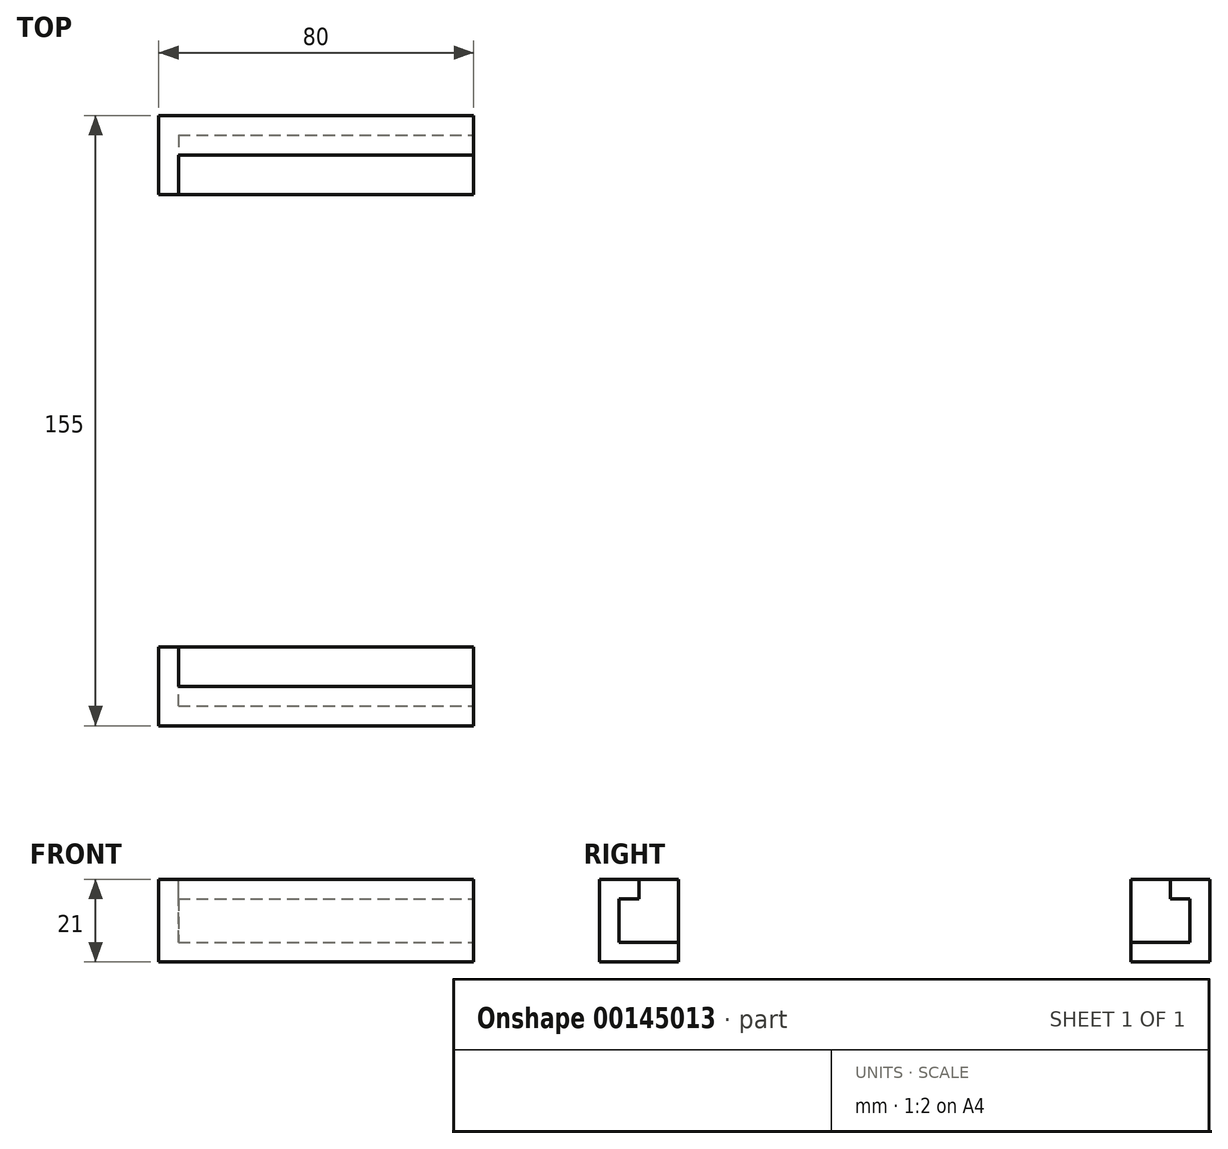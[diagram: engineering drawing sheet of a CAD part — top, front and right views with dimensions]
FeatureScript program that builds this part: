
annotation { "Feature Type Name" : "Feature", "Feature Type Description" : "" }
export const myFeature = defineFeature(function(context is Context, id is Id, definition is map)
    precondition{}
    {
        {
            var Q0;
            Q0=qCreatedBy(makeId("Top.planeOp"),FACE);
            var sketch = newSketch(context, id + "F0", { "sketchPlane" : qUnion([Q0])});
            skLineSegment(sketch, "E0.bottom", {"start": v(37.5, 77.5) * mm, "end": v(-37.5, 77.5) * mm});
            skLineSegment(sketch, "E0.top", {"start": v(37.5, -77.5) * mm, "end": v(-37.5, -77.5) * mm});
            skLineSegment(sketch, "E0.left", {"start": v(37.5, 77.5) * mm, "end": v(37.5, -77.5) * mm});
            skLineSegment(sketch, "E0.right", {"start": v(-37.5, 77.5) * mm, "end": v(-37.5, -77.5) * mm});
            skPoint(sketch, "E0.middle", {"position": v(0, 0) * mm});
            skSolve(sketch);
        }
        {
            var Q0;
            Q0 = qSketchRegion(id + "F0", true);
            extrude(context, id + "F1", {"entities" : qUnion([Q0]), "depth" : 5 * mm});
        }
        {
            var Q0;
            Q0=makeQuery(id+"F1.opExtrude","CAP_FACE",FACE,{"disambiguationData":[OSD([sQuery(id+"F0.wireOp",EDGE,"E0.bottom"),sQuery(id+"F0.wireOp",EDGE,"E0.top"),sQuery(id+"F0.wireOp",EDGE,"E0.left"),sQuery(id+"F0.wireOp",EDGE,"E0.right")])],"isStart":false});
            var sketch = newSketch(context, id + "F2", { "sketchPlane" : qUnion([Q0])});
            skLineSegment(sketch, "E1.bottom", {"start": v(-37.5, -77.5) * mm, "end": v(37.5, -77.5) * mm});
            skLineSegment(sketch, "E1.top", {"start": v(-37.5, -72.5) * mm, "end": v(37.5, -72.5) * mm});
            skLineSegment(sketch, "E1.left", {"start": v(-37.5, -77.5) * mm, "end": v(-37.5, -72.5) * mm});
            skLineSegment(sketch, "E1.right", {"start": v(37.5, -77.5) * mm, "end": v(37.5, -72.5) * mm});
            skSolve(sketch);
        }
        {
            var Q0;
            Q0 = qSketchRegion(id + "F2", true);
            extrude(context, id + "F3", {"entities" : qUnion([Q0]), "operationType" : NewBodyOperationType.ADD, "depth" : 11 * mm});
        }
        {
            var Q0;
            Q0=makeQuery(id+"F3.opExtrude","SWEPT_FACE",FACE,{"disambiguationData":[OSD([sQuery(id+"F2.wireOp",EDGE,"E1.top")])]});
            var sketch = newSketch(context, id + "F4", { "sketchPlane" : qUnion([Q0])});
            skLineSegment(sketch, "E2.bottom", {"start": v(-37.5, 16) * mm, "end": v(37.5, 16) * mm});
            skLineSegment(sketch, "E2.top", {"start": v(-37.5, 21) * mm, "end": v(37.5, 21) * mm});
            skLineSegment(sketch, "E2.left", {"start": v(-37.5, 16) * mm, "end": v(-37.5, 21) * mm});
            skLineSegment(sketch, "E2.right", {"start": v(37.5, 16) * mm, "end": v(37.5, 21) * mm});
            skSolve(sketch);
        }
        {
            var Q0;
            Q0 = qSketchRegion(id + "F4", true);
            extrude(context, id + "F5", {"entities" : qUnion([Q0]), "depth" : 5 * mm});
        }
        {
            var Q0;
            Q0=makeQuery(id+"F5.opExtrude","CAP_FACE",FACE,{"disambiguationData":[OSD([sQuery(id+"F4.wireOp",EDGE,"E2.bottom"),sQuery(id+"F4.wireOp",EDGE,"E2.top"),sQuery(id+"F4.wireOp",EDGE,"E2.left"),sQuery(id+"F4.wireOp",EDGE,"E2.right")])],"isStart":true});
            extrude(context, id + "F6", {"entities" : qUnion([Q0]), "depth" : 5 * mm});
        }
        {
            var Q0;
            Q0=makeQuery(id+"F6.opExtrude","SWEPT_BODY",BODY,{"disambiguationData":[OSD([sQuery(id+"F4.wireOp",EDGE,"E2.bottom"),sQuery(id+"F4.wireOp",EDGE,"E2.top"),sQuery(id+"F4.wireOp",EDGE,"E2.left"),sQuery(id+"F4.wireOp",EDGE,"E2.right")])]});
            var Q1;
            Q1=makeQuery(id+"F5.opExtrude","SWEPT_BODY",BODY,{"disambiguationData":[OSD([sQuery(id+"F4.wireOp",EDGE,"E2.bottom"),sQuery(id+"F4.wireOp",EDGE,"E2.top"),sQuery(id+"F4.wireOp",EDGE,"E2.left"),sQuery(id+"F4.wireOp",EDGE,"E2.right")])]});
            var Q2;
            Q2=makeQuery(id+"F1.opExtrude","SWEPT_BODY",BODY,{"disambiguationData":[OSD([sQuery(id+"F0.wireOp",EDGE,"E0.bottom"),sQuery(id+"F0.wireOp",EDGE,"E0.top"),sQuery(id+"F0.wireOp",EDGE,"E0.left"),sQuery(id+"F0.wireOp",EDGE,"E0.right")])]});
            booleanBodies(context, id + "F7", {"operationType" : BooleanOperationType.UNION, "tools" : qUnion([Q0, Q1, Q2])});
        }
        {
            var Q0;
            Q0=makeQuery(id+"F1.opExtrude","CAP_FACE",FACE,{"disambiguationData":[OSD([sQuery(id+"F0.wireOp",EDGE,"E0.bottom"),sQuery(id+"F0.wireOp",EDGE,"E0.top"),sQuery(id+"F0.wireOp",EDGE,"E0.left"),sQuery(id+"F0.wireOp",EDGE,"E0.right")])],"isStart":false});
            var sketch = newSketch(context, id + "F8", { "sketchPlane" : qUnion([Q0])});
            skLineSegment(sketch, "E3.bottom", {"start": v(-37.5, 77.5) * mm, "end": v(37.5, 77.5) * mm});
            skLineSegment(sketch, "E3.top", {"start": v(-37.5, 72.5) * mm, "end": v(37.5, 72.5) * mm});
            skLineSegment(sketch, "E3.left", {"start": v(-37.5, 77.5) * mm, "end": v(-37.5, 72.5) * mm});
            skLineSegment(sketch, "E3.right", {"start": v(37.5, 77.5) * mm, "end": v(37.5, 72.5) * mm});
            skSolve(sketch);
        }
        {
            var Q0;
            Q0 = qSketchRegion(id + "F8", true);
            extrude(context, id + "F9", {"entities" : qUnion([Q0]), "operationType" : NewBodyOperationType.ADD, "depth" : 11 * mm});
        }
        {
            var Q0;
            Q0=makeQuery(id+"F9.boolean.opBoolean","MERGE",FACE,{"derivedFrom":[makeQuery(id+"F1.opExtrude","SWEPT_FACE",FACE,{"disambiguationData":[OSD([sQuery(id+"F0.wireOp",EDGE,"E0.bottom")])]}),makeQuery(id+"F9.opExtrude","SWEPT_FACE",FACE,{"disambiguationData":[OSD([sQuery(id+"F8.wireOp",EDGE,"E3.bottom")])]})]});
            var sketch = newSketch(context, id + "F10", { "sketchPlane" : qUnion([Q0])});
            skLineSegment(sketch, "E4.bottom", {"start": v(-37.5, 16) * mm, "end": v(37.5, 16) * mm});
            skLineSegment(sketch, "E4.top", {"start": v(-37.5, 21) * mm, "end": v(37.5, 21) * mm});
            skLineSegment(sketch, "E4.left", {"start": v(-37.5, 16) * mm, "end": v(-37.5, 21) * mm});
            skLineSegment(sketch, "E4.right", {"start": v(37.5, 16) * mm, "end": v(37.5, 21) * mm});
            skSolve(sketch);
        }
        {
            var Q0;
            Q0=makeQuery(id+"F10.imprint","IMPRINT",FACE,{"disambiguationData":[TD([[makeQuery(id+"F10.imprint","IMPRINT",EDGE,{"derivedFrom":sQuery(id+"F10.wireOp",EDGE,"E4.bottom")}),1.0]])]});
            extrude(context, id + "F11", {"entities" : qUnion([Q0]), "operationType" : NewBodyOperationType.ADD, "oppositeDirection" : true, "depth" : 10 * mm});
        }
        {
            var Q0;
            Q0=makeQuery(id+"F1.opExtrude","CAP_FACE",FACE,{"disambiguationData":[OSD([sQuery(id+"F0.wireOp",EDGE,"E0.bottom"),sQuery(id+"F0.wireOp",EDGE,"E0.top"),sQuery(id+"F0.wireOp",EDGE,"E0.left"),sQuery(id+"F0.wireOp",EDGE,"E0.right")])],"isStart":true});
            var sketch = newSketch(context, id + "F12", { "sketchPlane" : qUnion([Q0])});
            skLineSegment(sketch, "E5.bottom", {"start": v(-37.5, -77.5) * mm, "end": v(-42.5, -77.5) * mm});
            skLineSegment(sketch, "E5.top", {"start": v(-37.5, 77.5) * mm, "end": v(-42.5, 77.5) * mm});
            skLineSegment(sketch, "E5.left", {"start": v(-37.5, -77.5) * mm, "end": v(-37.5, 77.5) * mm});
            skLineSegment(sketch, "E5.right", {"start": v(-42.5, -77.5) * mm, "end": v(-42.5, 77.5) * mm});
            skSolve(sketch);
        }
        {
            var Q0;
            Q0 = qSketchRegion(id + "F12", true);
            var Q1;
            {var subQ0=sQuery(id+"F4.wireOp",EDGE,"E2.top");Q1=makeQuery(id+"F7.opBoolean","MERGE",FACE,{"derivedFrom":[makeQuery(id+"F5.opExtrude","SWEPT_FACE",FACE,{"disambiguationData":[OSD([subQ0])]}),makeQuery(id+"F6.opExtrude","SWEPT_FACE",FACE,{"disambiguationData":[OSD([subQ0])]})]});}
            extrude(context, id + "F13", {"entities" : qUnion([Q0]), "operationType" : NewBodyOperationType.ADD, "endBound" : BoundingType.UP_TO_SURFACE, "oppositeDirection" : true, "endBoundEntityFace" : qUnion([Q1]), "depth" : 20 * mm});
        }
        {
            var Q0;
            Q0=makeQuery(id+"F1.opExtrude","CAP_FACE",FACE,{"disambiguationData":[OSD([sQuery(id+"F0.wireOp",EDGE,"E0.bottom"),sQuery(id+"F0.wireOp",EDGE,"E0.top"),sQuery(id+"F0.wireOp",EDGE,"E0.left"),sQuery(id+"F0.wireOp",EDGE,"E0.right")])],"isStart":false});
            var sketch = newSketch(context, id + "F14", { "sketchPlane" : qUnion([Q0])});
            skLineSegment(sketch, "E6.bottom", {"start": v(-105.78, 57.5) * mm, "end": v(105.78, 57.5) * mm});
            skLineSegment(sketch, "E6.top", {"start": v(-105.78, -57.5) * mm, "end": v(105.78, -57.5) * mm});
            skLineSegment(sketch, "E6.left", {"start": v(-105.78, 57.5) * mm, "end": v(-105.78, -57.5) * mm});
            skLineSegment(sketch, "E6.right", {"start": v(105.78, 57.5) * mm, "end": v(105.78, -57.5) * mm});
            skPoint(sketch, "E6.middle", {"position": v(0, 0) * mm});
            skSolve(sketch);
        }
        {
            var Q0;
            Q0 = qSketchRegion(id + "F14", true);
            extrude(context, id + "F15", {"entities" : qUnion([Q0]), "operationType" : NewBodyOperationType.REMOVE, "endBound" : BoundingType.THROUGH_ALL, "oppositeDirection" : true, "depth" : 25 * mm});
        }
        {
            var Q0;
            Q0 = qSketchRegion(id + "F14", true);
            extrude(context, id + "F16", {"entities" : qUnion([Q0]), "operationType" : NewBodyOperationType.REMOVE, "depth" : 25 * mm});
        }
    });
